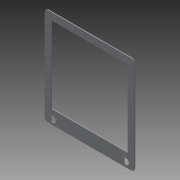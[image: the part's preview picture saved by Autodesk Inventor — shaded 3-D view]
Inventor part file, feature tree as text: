
AUTODESK INVENTOR PART (.ipt)
format: ipt  version: 2014 SP1 (Build 180222100, 222)  size: 181,248 bytes
history: native  units: mm
features: extrude x1, sketch x1
ambient origin geometry x8: Origin, YZ Plane, XZ Plane, XY Plane, X Axis, Y Axis, Z Axis, Center Point
bodies: Solid1 (feature_tree)
feature tree (2):
  extrude  "Extrusion1"  [1 undecoded]
  sketch  "Sketch2"  dims[d0=4.0mm d1=0.0mm]
note: 1 required parameter value undecoded (feature->parameter linkage not recoverable at this tier; creation-order binding heuristic only, values carry confidence <= 0.55)
